# Revit family: Gira_5500000
name_source: partatom
category: Electrical Fixtures
revit_build: Autodesk Revit 2017 (Build: 20160225_1515(x64)
units: mm (PartAtom-declared; Revit-internal decimal feet)

## family parameters
Cut with Voids When Loaded = No
Host = Face
Maintain Annotation Orientation = No
Part Type = Normal
Room Calculation Point = No
Round Connector Dimension = Use Diameter
Shared = No

## types (1)
- DCS-IP data I/F Door communication
    App control via Bluetooth = No
    Applicable with button = No
    Applicable with infrared button = No
    Applicable with movement sensor = No
    Applicable with presence indicator = No
    Applicable with time switch/timer = No
    Applicable with transmission button = No
    BIM = https://media.live.bim.site X1 REG KNX.rfa
    BIMSITE_PRODUCT_ID = 25b31a60b08b35c61d503afbc6bb24e588bc6163
    Bus connection included = No
    Cost = 0 $
    Default Elevation = 1219 mm
    Description = DCS-IP data I F Door DCS-IP data interface, Features: - The data interface is used to expand the current push-button start-up procedure by adding convenient start-up via PC laptop and to connect the 2-wire bus to IP. - Configuration via Gira Project Assistant (GPA). - Commissioning of large projects. - Reading out of the configuration data of existing systems. - Connection of Gira 2-wire bus to IP. - Only suitable for indoor use.
    Dimming phase cut-off = No
    Dimming phase cut-on = No
    GTIN = 4010337052685
    HAN = 5500000
    Halogen free = No
    HeinzeBIM = https://www.heinze.de
    Light value memory = No
    Local operation/hand operation = No
    Manufacturer = Gira
    Max. number of venetian-blind outputs = 0
    Max. switching power [Voltampere] = 0
    Modulare Erweiterungsmöglichkeit = No
    Number of binary inputs = 0
    Number of inputs = 0
    Number of outputs = 0
    Parallel-service possible = No
    Power boost suitable = No
    Radio frequent bidirectional = No
    Serial dimmer = No
    Suitable for C-load = No
    Transparent = No
    URL = https://www.gira.de
    Verschiedene Phasen anschließbar = No
    With label area = No
    With switch function = No

## geometry (parser evidence)
native form markers: Blend x2, Sweep x3
no freeform markers — native parametric forms only
